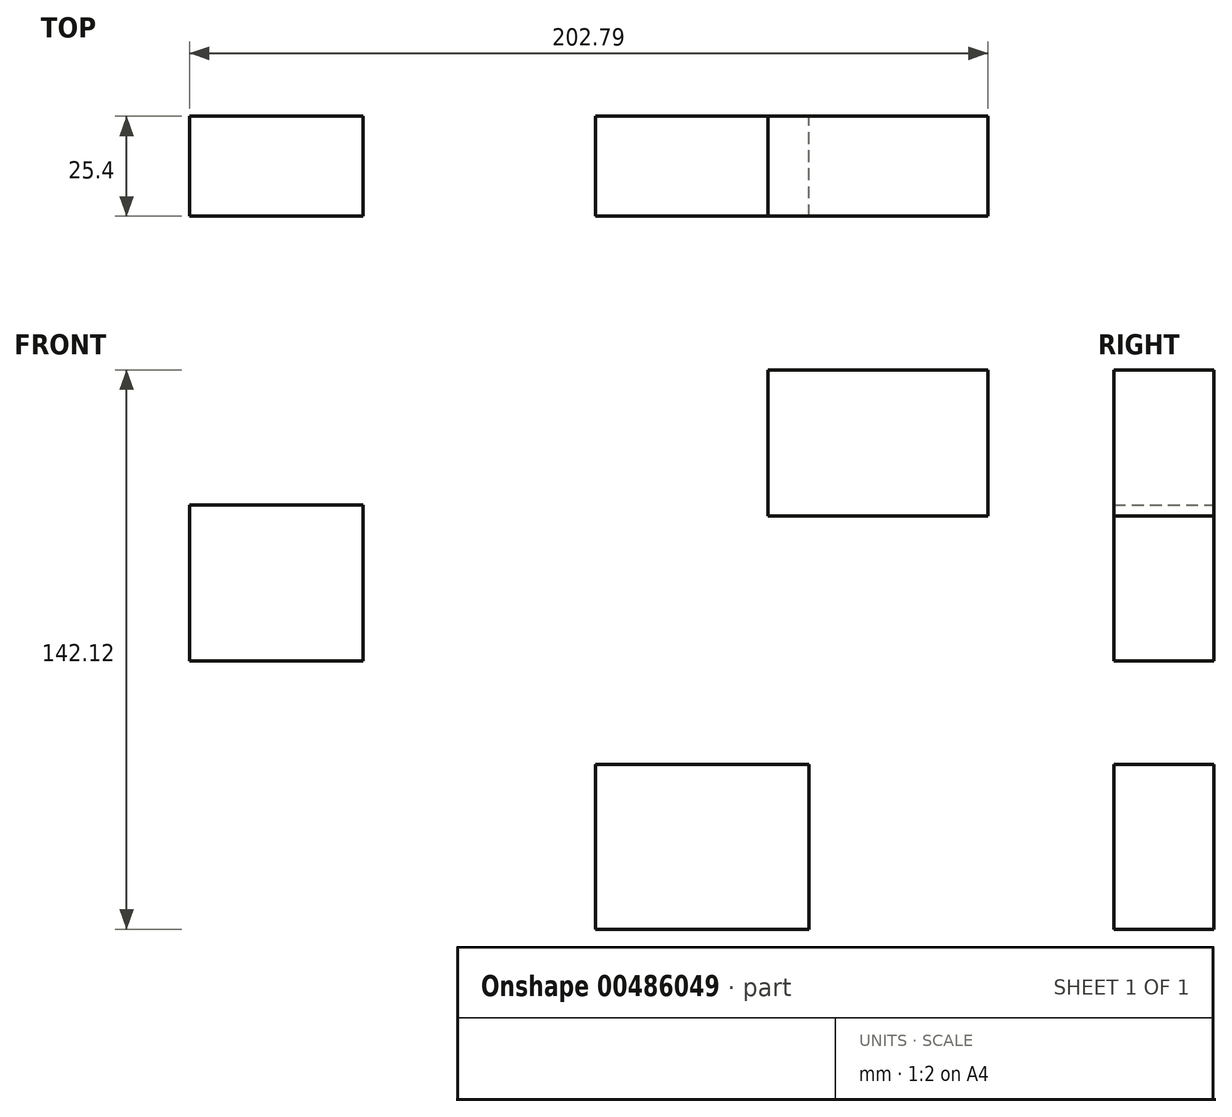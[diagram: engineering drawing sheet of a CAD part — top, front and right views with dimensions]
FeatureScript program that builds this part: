
annotation { "Feature Type Name" : "Feature", "Feature Type Description" : "" }
export const myFeature = defineFeature(function(context is Context, id is Id, definition is map)
    precondition{}
    {
        {
            var Q0;
            Q0=qCreatedBy(makeId("Front.planeOp"),FACE);
            var sketch = newSketch(context, id + "F0", { "sketchPlane" : qUnion([Q0])});
            skLineSegment(sketch, "E0.bottom", {"start": v(-103.13, 20.35) * mm, "end": v(-59.1, 20.35) * mm});
            skLineSegment(sketch, "E0.top", {"start": v(-103.13, -19.38) * mm, "end": v(-59.1, -19.38) * mm});
            skLineSegment(sketch, "E0.left", {"start": v(-103.13, 20.35) * mm, "end": v(-103.13, -19.38) * mm});
            skLineSegment(sketch, "E0.right", {"start": v(-59.1, 20.35) * mm, "end": v(-59.1, -19.38) * mm});
            skLineSegment(sketch, "E1.bottom", {"start": v(0, -45.64) * mm, "end": v(54.17, -45.64) * mm});
            skLineSegment(sketch, "E1.top", {"start": v(0, -87.5) * mm, "end": v(54.17, -87.5) * mm});
            skLineSegment(sketch, "E1.left", {"start": v(0, -45.64) * mm, "end": v(0, -87.5) * mm});
            skLineSegment(sketch, "E1.right", {"start": v(54.17, -45.64) * mm, "end": v(54.17, -87.5) * mm});
            skLineSegment(sketch, "E2.bottom", {"start": v(43.74, 54.63) * mm, "end": v(99.66, 54.63) * mm});
            skLineSegment(sketch, "E2.top", {"start": v(43.74, 17.47) * mm, "end": v(99.66, 17.47) * mm});
            skLineSegment(sketch, "E2.left", {"start": v(43.74, 54.63) * mm, "end": v(43.74, 17.47) * mm});
            skLineSegment(sketch, "E2.right", {"start": v(99.66, 54.63) * mm, "end": v(99.66, 17.47) * mm});
            skSolve(sketch);
        }
        {
            var Q0;
            Q0 = qSketchRegion(id + "F0", true);
            extrude(context, id + "F1", {"entities" : qUnion([Q0]), "depth" : 25.4 * mm});
        }
    });
